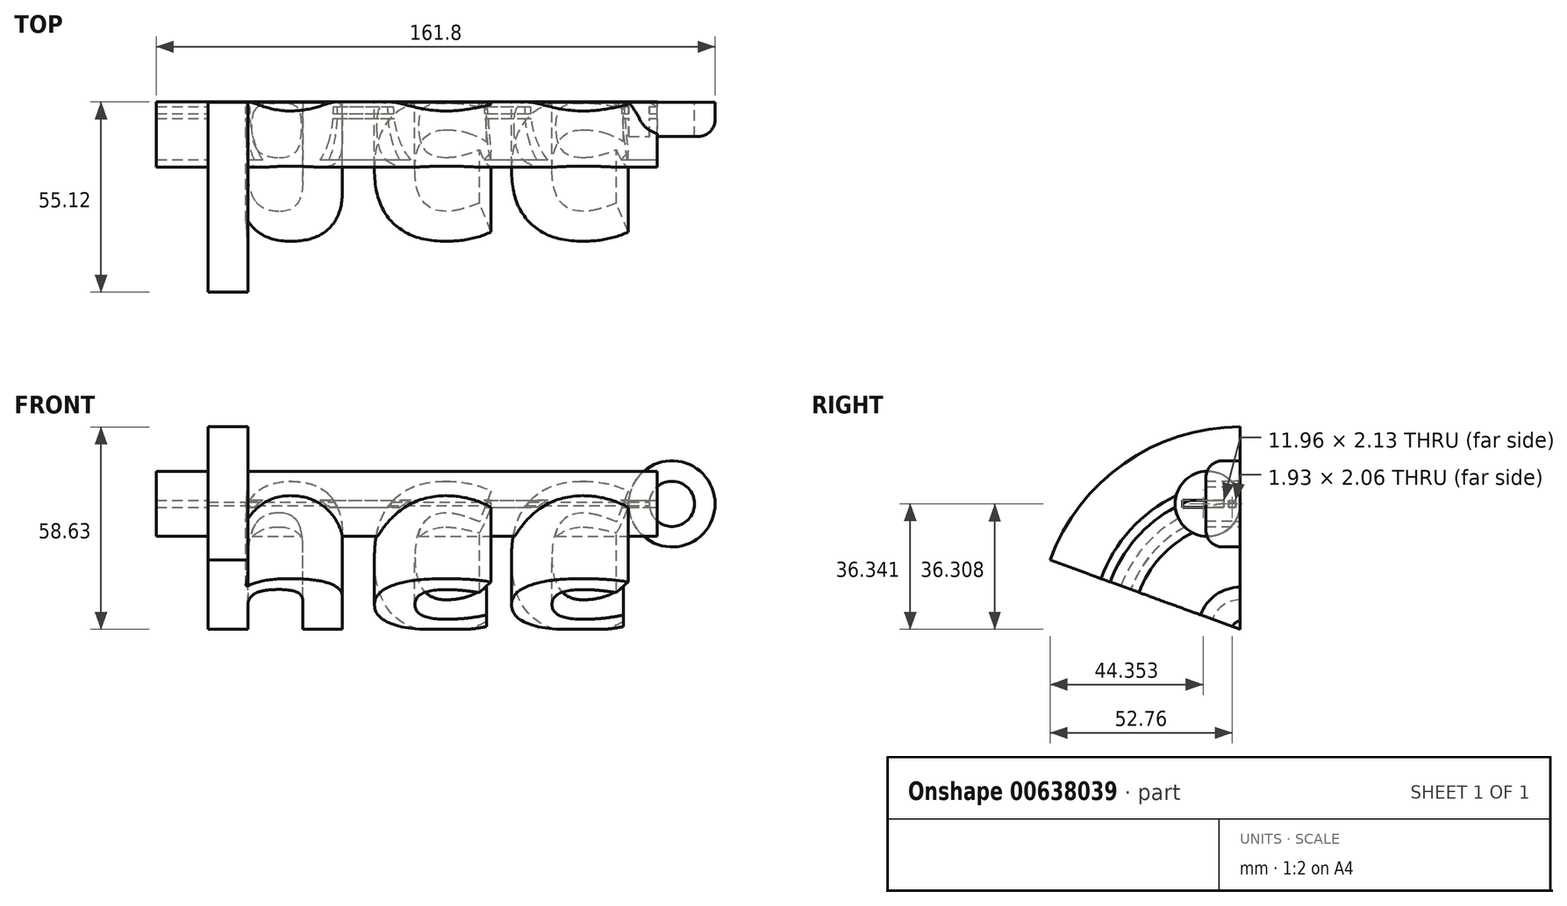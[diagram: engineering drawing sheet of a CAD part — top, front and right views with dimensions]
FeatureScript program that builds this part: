
annotation { "Feature Type Name" : "Feature", "Feature Type Description" : "" }
export const myFeature = defineFeature(function(context is Context, id is Id, definition is map)
    precondition{}
    {
        {
            var Q0;
            Q0=qCreatedBy(makeId("Front.planeOp"),FACE);
            var sketch = newSketch(context, id + "F0", { "sketchPlane" : qUnion([Q0])});
            skText(sketch, "E0", { "text": "hcc", "fontName": "OpenSans-Bold.ttf"});
            skLineSegment(sketch, "E1", {"start": v(-64.26, -0.06) * mm, "end": v(68.4, -0.06) * mm});
            const initialGuessF0  = {"E0": [-0.06426, -6e-05, 1, 0, 0.05556]};
            skSetInitialGuess(sketch, initialGuessF0);
            skSolve(sketch);
        }
        {
            var Q0;
            {var subQ2=sQuery(id+"F0.wireOp",EDGE,"E0.sketch_text.stroke-1");Q0=makeQuery(id+"F0.imprint","IMPRINT",FACE,{"disambiguationData":[TD([[makeQuery(id+"F0.imprint","IMPRINT",EDGE,{"derivedFrom":subQ2}),-1.0]])]});}
            var Q1;
            {var subQ0=sQuery(id+"F0.wireOp",EDGE,"E0.sketch_text.stroke-18");Q1=makeQuery(id+"F0.imprint","IMPRINT",FACE,{"disambiguationData":[TD([[makeQuery(id+"F0.imprint","IMPRINT",EDGE,{"derivedFrom":subQ0}),-1.0]])]});}
            var Q2;
            {var subQ0=sQuery(id+"F0.wireOp",EDGE,"E0.sketch_text.stroke-32");Q2=makeQuery(id+"F0.imprint","IMPRINT",FACE,{"disambiguationData":[TD([[makeQuery(id+"F0.imprint","IMPRINT",EDGE,{"derivedFrom":subQ0}),-1.0]])]});}
            var Q3;
            Q3=sQuery(id+"F0.wireOp",EDGE,"E1");
            revolve(context, id + "F1", {"entities" : qUnion([Q0, Q1, Q2]), "axis" : qUnion([Q3]), "revolveType" : RevolveType.ONE_DIRECTION, "angle" : 70 * degree});
        }
        {
            var Q0;
            Q0=makeQuery(id+"F1.opRevolve","SWEPT_FACE",FACE,{"disambiguationData":[OSD([sQuery(id+"F0.wireOp",EDGE,"E0.sketch_text.stroke-7")])]});
            var sketch = newSketch(context, id + "F2", { "sketchPlane" : qUnion([Q0])});
            skCircle(sketch, "E2", {"center": v(9.42, 36.28) * mm, "radius": 9.43 * mm});
            skLineSegment(sketch, "E3.bottom", {"start": v(4.77, 37.34) * mm, "end": v(16.73, 37.34) * mm});
            skLineSegment(sketch, "E3.top", {"start": v(4.77, 35.22) * mm, "end": v(16.73, 35.22) * mm});
            skLineSegment(sketch, "E3.left", {"start": v(4.77, 37.34) * mm, "end": v(4.77, 35.22) * mm});
            skLineSegment(sketch, "E3.right", {"start": v(16.73, 37.34) * mm, "end": v(16.73, 35.22) * mm});
            skLineSegment(sketch, "E4.bottom", {"start": v(3.3, 37.28) * mm, "end": v(1.38, 37.28) * mm});
            skLineSegment(sketch, "E4.top", {"start": v(3.3, 35.22) * mm, "end": v(1.38, 35.22) * mm});
            skLineSegment(sketch, "E4.left", {"start": v(3.3, 37.28) * mm, "end": v(3.3, 35.22) * mm});
            skLineSegment(sketch, "E4.right", {"start": v(1.38, 37.28) * mm, "end": v(1.38, 35.22) * mm});
            skPoint(sketch, "E5", {"position": v(4.77, 36.28) * mm});
            skSolve(sketch);
        }
        {
            var Q0;
            Q0=makeQuery(id+"F2.imprint","IMPRINT",FACE,{"disambiguationData":[TD([[makeQuery(id+"F2.imprint","IMPRINT",EDGE,{"derivedFrom":sQuery(id+"F2.wireOp",EDGE,"E2")}),1.0]])]});
            var Q1;
            Q1=makeQuery(id+"F2.imprint","IMPRINT",FACE,{"disambiguationData":[TD([[makeQuery(id+"F2.imprint","IMPRINT",EDGE,{"derivedFrom":sQuery(id+"F2.wireOp",EDGE,"E3.bottom")}),1.0]])]});
            extrude(context, id + "F3", {"entities" : qUnion([Q0, Q1]), "operationType" : NewBodyOperationType.ADD, "depth" : 15 * mm, "offsetDistance" : 25 * mm, "hasSecondDirection" : true, "secondDirectionOppositeDirection" : true, "secondDirectionDepth" : 130 * mm});
        }
        {
            var Q0;
            Q0=qCreatedBy(makeId("Front.planeOp"),FACE);
            var sketch = newSketch(context, id + "F4", { "sketchPlane" : qUnion([Q0])});
            skCircle(sketch, "E6", {"center": v(76.07, 36.27) * mm, "radius": 12.5 * mm});
            skCircle(sketch, "E7", {"center": v(76.07, 36.27) * mm, "radius": 6.55 * mm});
            skSolve(sketch);
        }
        {
            var Q0;
            Q0=makeQuery(id+"F4.imprint","IMPRINT",FACE,{"disambiguationData":[TD([[makeQuery(id+"F4.imprint","IMPRINT",EDGE,{"derivedFrom":sQuery(id+"F4.wireOp",EDGE,"E6")}),1.0]])]});
            extrude(context, id + "F5", {"entities" : qUnion([Q0]), "operationType" : NewBodyOperationType.ADD, "depth" : 10 * mm, "offsetDistance" : 25 * mm});
        }
        {
            var Q0;
            {var subQ0=sQuery(id+"F4.wireOp",EDGE,"E6");Q0=makeQuery(id+"F5.boolean.opBoolean","SPLIT",EDGE,{"disambiguationData":[TD([makeQuery(id+"F3.opExtrude","SWEPT_FACE",FACE,{"disambiguationData":[OSD([sQuery(id+"F2.wireOp",EDGE,"E2")])]})])],"derivedFrom":makeQuery(id+"F5.opExtrude","CAP_EDGE",EDGE,{"disambiguationData":[OSD([subQ0])],"isStart":false})});}
            fillet(context, id + "F6", {"entities" : qUnion([Q0]), "radius" : 5 * mm, "tangentPropagation" : true, "allowEdgeOverflow" : false});
        }
    });
